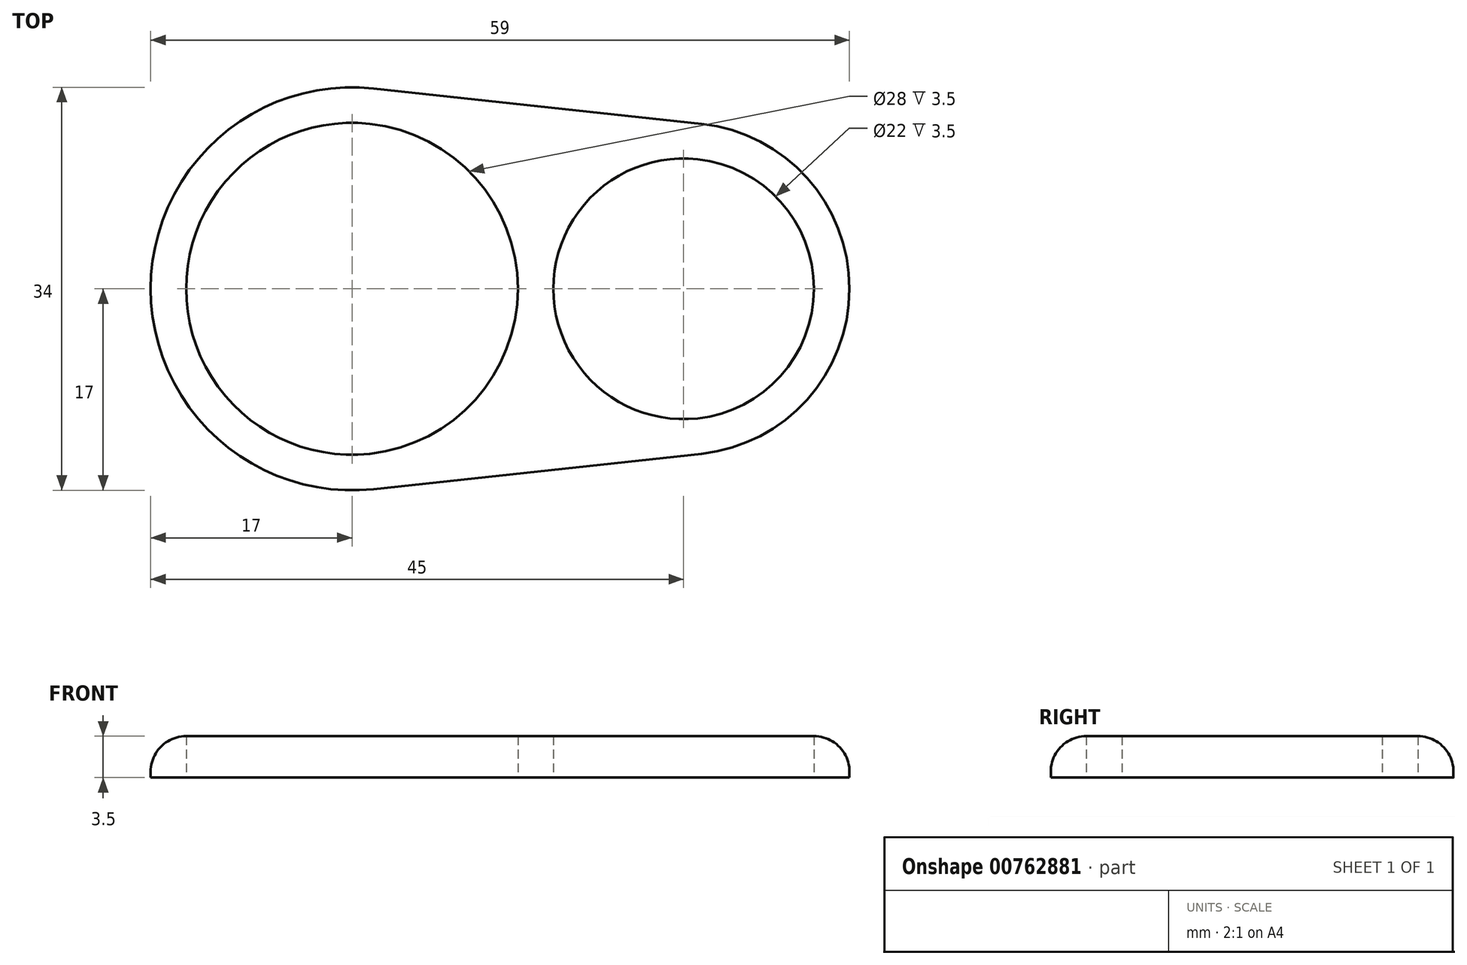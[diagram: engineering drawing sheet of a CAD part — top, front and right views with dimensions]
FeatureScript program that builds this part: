
annotation { "Feature Type Name" : "Feature", "Feature Type Description" : "" }
export const myFeature = defineFeature(function(context is Context, id is Id, definition is map)
    precondition{}
    {
        {
            var Q0;
            Q0=qCreatedBy(makeId("Top.planeOp"),FACE);
            var sketch = newSketch(context, id + "F0", { "sketchPlane" : qUnion([Q0])});
            skArc(sketch, "E0", {"start": v(1.82, 16.9) * mm, "mid": v(-17, 0) * mm, "end": v(1.82, -16.9) * mm});
            skCircle(sketch, "E1", {"center": v(0, 0) * mm, "radius": 14 * mm});
            skCircle(sketch, "E2", {"center": v(28, 0) * mm, "radius": 11 * mm});
            skLineSegment(sketch, "E3", {"start": v(1.82, -16.9) * mm, "end": v(29.5, -13.92) * mm});
            skLineSegment(sketch, "E4.MirrorCS", {"start": v(1.82, 16.9) * mm, "end": v(29.5, 13.92) * mm});
            skArc(sketch, "E5.trimOffspring", {"start": v(29.5, -13.92) * mm, "mid": v(42, 0) * mm, "end": v(29.5, 13.92) * mm});
            skLineSegment(sketch, "E6", {"start": v(-17, 0) * mm, "end": v(42, 0) * mm});
            skSolve(sketch);
        }
        {
            var Q0;
            Q0=makeQuery(id+"F0.imprint","IMPRINT",FACE,{"disambiguationData":[TD([[makeQuery(id+"F0.imprint","IMPRINT",EDGE,{"derivedFrom":sQuery(id+"F0.wireOp",EDGE,"E0")}),1.0]])]});
            extrude(context, id + "F1", {"entities" : qUnion([Q0]), "depth" : 3.5 * mm, "offsetDistance" : 25 * mm});
        }
        {
            var Q0;
            Q0=makeQuery(id+"F1.opExtrude","CAP_EDGE",EDGE,{"disambiguationData":[OSD([sQuery(id+"F0.wireOp",EDGE,"E3")])],"isStart":false});
            fillet(context, id + "F2", {"entities" : qUnion([Q0]), "radius" : 3 * mm, "tangentPropagation" : true, "allowEdgeOverflow" : false});
        }
    });
